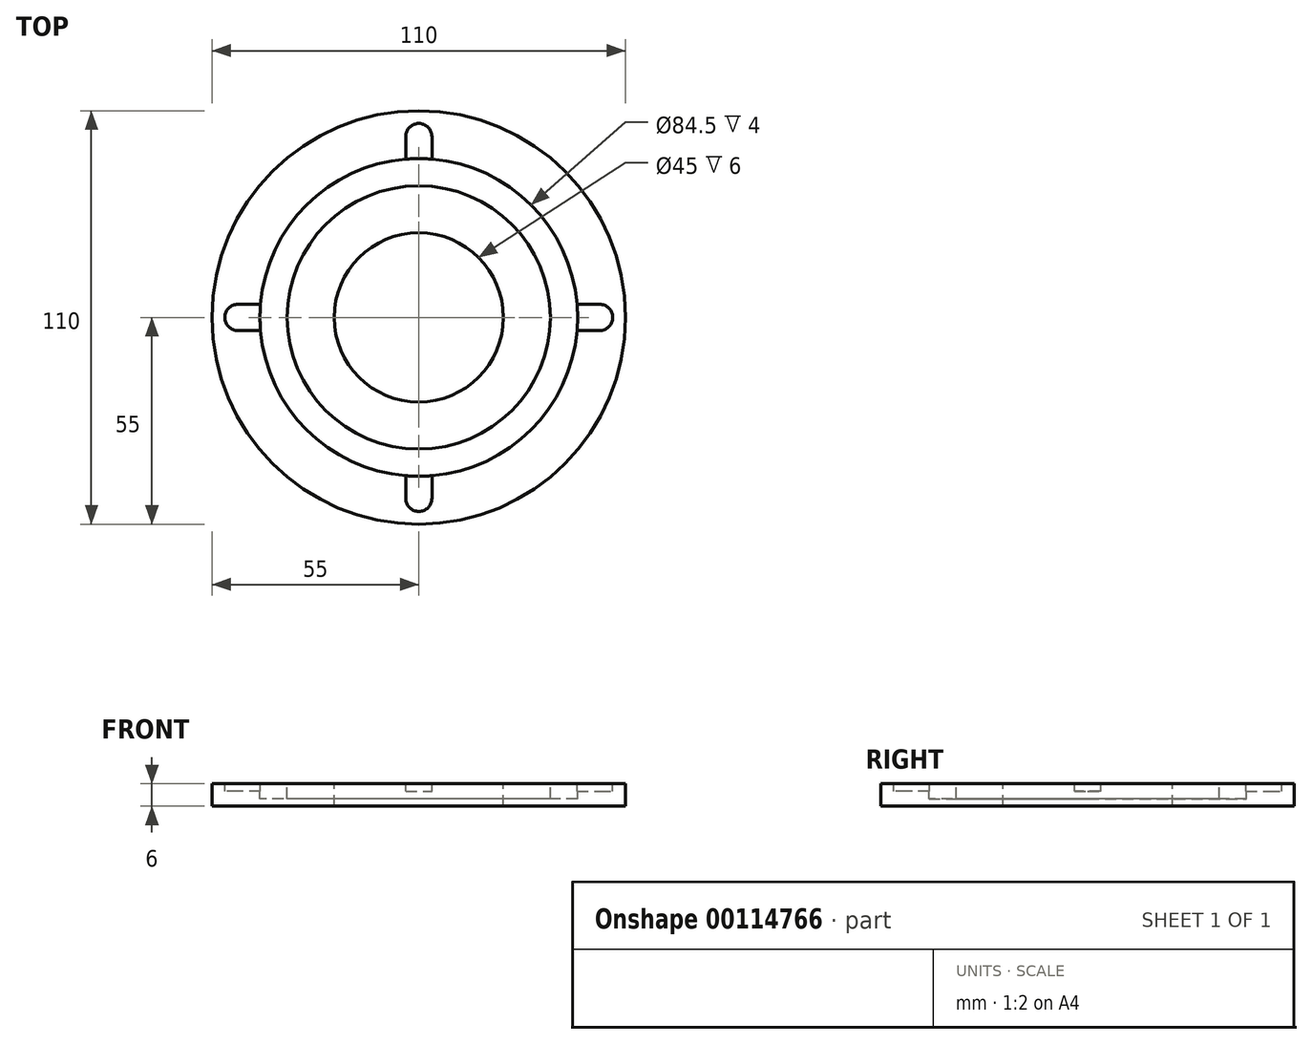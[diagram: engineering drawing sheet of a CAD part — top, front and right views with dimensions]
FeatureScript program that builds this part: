
annotation { "Feature Type Name" : "Feature", "Feature Type Description" : "" }
export const myFeature = defineFeature(function(context is Context, id is Id, definition is map)
    precondition{}
    {
        {
            var Q0;
            Q0=qCreatedBy(makeId("Top.planeOp"),FACE);
            var sketch = newSketch(context, id + "F0", { "sketchPlane" : qUnion([Q0])});
            skCircle(sketch, "E0", {"center": v(0, 0) * mm, "radius": 55 * mm});
            skSolve(sketch);
        }
        {
            var Q0;
            Q0 = qSketchRegion(id + "F0", true);
            extrude(context, id + "F1", {"entities" : qUnion([Q0]), "depth" : 6 * mm});
        }
        {
            var Q0;
            Q0=makeQuery(id+"F1.opExtrude","CAP_FACE",FACE,{"disambiguationData":[OSD([sQuery(id+"F0.wireOp",EDGE,"E0")])],"isStart":false});
            var sketch = newSketch(context, id + "F2", { "sketchPlane" : qUnion([Q0])});
            skCircle(sketch, "E1", {"center": v(0, 0) * mm, "radius": 42.25 * mm});
            skCircle(sketch, "E2", {"center": v(0, 0) * mm, "radius": 35 * mm});
            skSolve(sketch);
        }
        {
            var Q0;
            Q0 = qSketchRegion(id + "F2", true);
            extrude(context, id + "F3", {"entities" : qUnion([Q0]), "operationType" : NewBodyOperationType.REMOVE, "oppositeDirection" : true, "depth" : 4 * mm});
        }
        {
            var Q0;
            {var subQ0=sQuery(id+"F0.wireOp",EDGE,"E0");Q0=makeQuery(id+"F3.boolean.opBoolean","SPLIT",FACE,{"disambiguationData":[TD([makeQuery(id+"F1.opExtrude","SWEPT_FACE",FACE,{"disambiguationData":[OSD([subQ0])]})])],"derivedFrom":makeQuery(id+"F1.opExtrude","CAP_FACE",FACE,{"disambiguationData":[OSD([subQ0])],"isStart":false})});}
            var sketch = newSketch(context, id + "F4", { "sketchPlane" : qUnion([Q0])});
            skLineSegment(sketch, "E3", {"start": v(-3.5, 42.1) * mm, "end": v(-3.5, 48.1) * mm});
            skLineSegment(sketch, "E4", {"start": v(3.5, 48.1) * mm, "end": v(3.5, 42.1) * mm});
            skArc(sketch, "E5", {"start": v(3.5, 48.1) * mm, "mid": v(0, 51.6) * mm, "end": v(-3.5, 48.1) * mm});
            skArc(sketch, "E6", {"start": v(3.5, 42.1) * mm, "mid": v(0, 42.25) * mm, "end": v(-3.5, 42.1) * mm});
            skLineSegment(sketch, "E7.1.0", {"start": v(-42.1, -3.5) * mm, "end": v(-48.1, -3.5) * mm});
            skArc(sketch, "E7.1.1", {"start": v(-48.1, 3.5) * mm, "mid": v(-51.6, 0) * mm, "end": v(-48.1, -3.5) * mm});
            skLineSegment(sketch, "E7.1.2", {"start": v(-48.1, 3.5) * mm, "end": v(-42.1, 3.5) * mm});
            skArc(sketch, "E7.1.3", {"start": v(-42.1, 3.5) * mm, "mid": v(-42.25, 0) * mm, "end": v(-42.1, -3.5) * mm});
            skLineSegment(sketch, "E7.2.0", {"start": v(3.5, -42.1) * mm, "end": v(3.5, -48.1) * mm});
            skArc(sketch, "E7.2.1", {"start": v(-3.5, -48.1) * mm, "mid": v(0, -51.6) * mm, "end": v(3.5, -48.1) * mm});
            skLineSegment(sketch, "E7.2.2", {"start": v(-3.5, -48.1) * mm, "end": v(-3.5, -42.1) * mm});
            skArc(sketch, "E7.2.3", {"start": v(-3.5, -42.1) * mm, "mid": v(0, -42.25) * mm, "end": v(3.5, -42.1) * mm});
            skLineSegment(sketch, "E7.3.0", {"start": v(42.1, 3.5) * mm, "end": v(48.1, 3.5) * mm});
            skArc(sketch, "E7.3.1", {"start": v(48.1, -3.5) * mm, "mid": v(51.6, 0) * mm, "end": v(48.1, 3.5) * mm});
            skLineSegment(sketch, "E7.3.2", {"start": v(48.1, -3.5) * mm, "end": v(42.1, -3.5) * mm});
            skArc(sketch, "E7.3.3", {"start": v(42.1, -3.5) * mm, "mid": v(42.25, 0) * mm, "end": v(42.1, 3.5) * mm});
            skSolve(sketch);
        }
        {
            var Q0;
            Q0 = qSketchRegion(id + "F4", true);
            extrude(context, id + "F5", {"entities" : qUnion([Q0]), "operationType" : NewBodyOperationType.REMOVE, "oppositeDirection" : true, "depth" : 2 * mm});
        }
        {
            var Q0;
            Q0=makeQuery(id+"F3.boolean.opBoolean","SPLIT",FACE,{"disambiguationData":[TD([makeQuery(id+"F3.opExtrude","SWEPT_FACE",FACE,{"disambiguationData":[OSD([sQuery(id+"F2.wireOp",EDGE,"E2")])]})])],"derivedFrom":makeQuery(id+"F1.opExtrude","CAP_FACE",FACE,{"disambiguationData":[OSD([sQuery(id+"F0.wireOp",EDGE,"E0")])],"isStart":false})});
            var sketch = newSketch(context, id + "F6", { "sketchPlane" : qUnion([Q0])});
            skCircle(sketch, "E8", {"center": v(0, 0) * mm, "radius": 22.5 * mm});
            skSolve(sketch);
        }
        {
            var Q0;
            Q0 = qSketchRegion(id + "F6", true);
            extrude(context, id + "F7", {"entities" : qUnion([Q0]), "operationType" : NewBodyOperationType.REMOVE, "endBound" : BoundingType.THROUGH_ALL, "oppositeDirection" : true, "depth" : 25 * mm});
        }
    });
